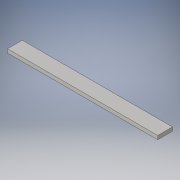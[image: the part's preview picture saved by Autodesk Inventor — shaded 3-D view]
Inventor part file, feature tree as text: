
AUTODESK INVENTOR PART (.ipt)
format: ipt  version: 2016 (Build 200138000, 138)  size: 86,528 bytes
history: native  units: in
note: dims shown in document units (in); Inventor stores cm internally (conversion verified against a paired STEP export)
features: extrude x1, sketch x1
ambient origin geometry x8: Origin, YZ Plane, XZ Plane, XY Plane, X Axis, Y Axis, Z Axis, Center Point
bodies: Solid1 (feature_tree)
feature tree (2):
  extrude  "Extrusion1"  Depth=0.125in TaperAngle=0.0deg
  sketch  "Sketch1"  dims[d0=5.0in d1=0.125in d2=0.0in]
